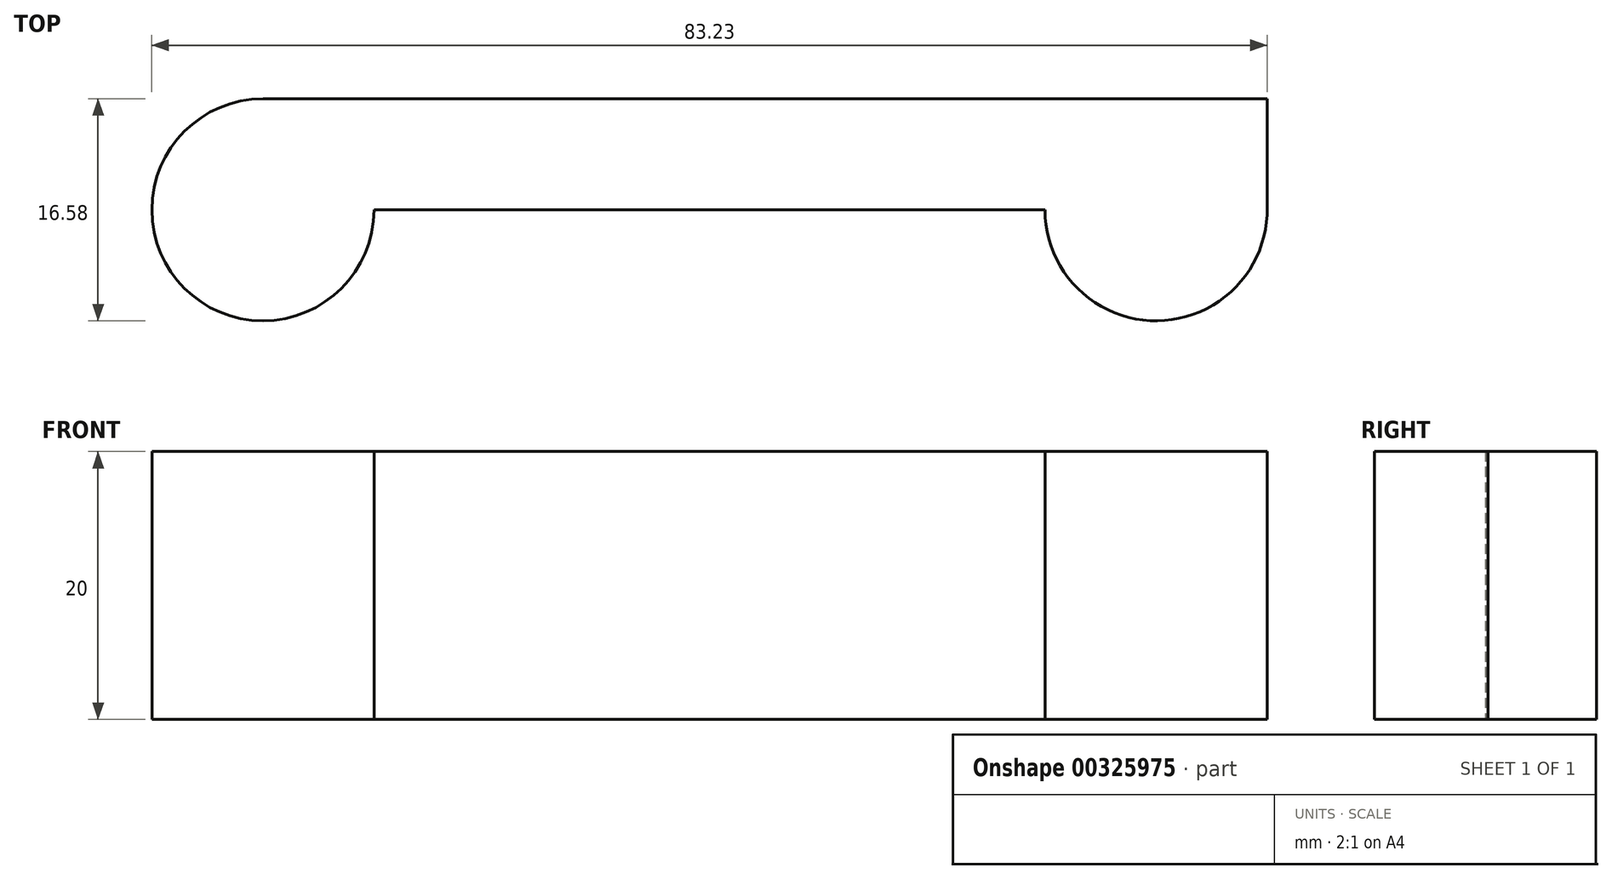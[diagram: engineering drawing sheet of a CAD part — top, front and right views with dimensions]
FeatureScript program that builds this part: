
annotation { "Feature Type Name" : "Feature", "Feature Type Description" : "" }
export const myFeature = defineFeature(function(context is Context, id is Id, definition is map)
    precondition{}
    {
        {
            var Q0;
            Q0=qCreatedBy(makeId("Top.planeOp"),FACE);
            var sketch = newSketch(context, id + "F0", { "sketchPlane" : qUnion([Q0])});
            skCircle(sketch, "E0", {"center": v(0, 0) * mm, "radius": 8.29 * mm});
            skLineSegment(sketch, "E1.bottom", {"start": v(0, 8.29) * mm, "end": v(74.94, 8.29) * mm});
            skLineSegment(sketch, "E1.top", {"start": v(0, 0) * mm, "end": v(74.94, 0) * mm});
            skLineSegment(sketch, "E1.left", {"start": v(0, 8.29) * mm, "end": v(0, 0) * mm});
            skLineSegment(sketch, "E1.right", {"start": v(74.94, 8.29) * mm, "end": v(74.94, 0) * mm});
            skCircle(sketch, "E2", {"center": v(66.65, 0) * mm, "radius": 8.29 * mm});
            skSolve(sketch);
        }
        {
            var Q0;
            {var subQ0=sQuery(id+"F0.wireOp",EDGE,"E1.left");Q0=makeQuery(id+"F0.imprint","IMPRINT",FACE,{"disambiguationData":[TD([[makeQuery(id+"F0.imprint","IMPRINT",EDGE,{"derivedFrom":subQ0}),-1.0]])]});}
            var Q1;
            {var subQ0=sQuery(id+"F0.wireOp",EDGE,"E1.left");Q1=makeQuery(id+"F0.imprint","IMPRINT",FACE,{"disambiguationData":[TD([[makeQuery(id+"F0.imprint","IMPRINT",EDGE,{"derivedFrom":subQ0}),1.0]])]});}
            extrude(context, id + "F1", {"entities" : qUnion([Q0, Q1]), "depth" : 20 * mm});
        }
        {
            var Q0;
            Q0 = qSketchRegion(id + "F0", true);
            extrude(context, id + "F2", {"entities" : qUnion([Q0]), "operationType" : NewBodyOperationType.ADD, "depth" : 20 * mm});
        }
    });
